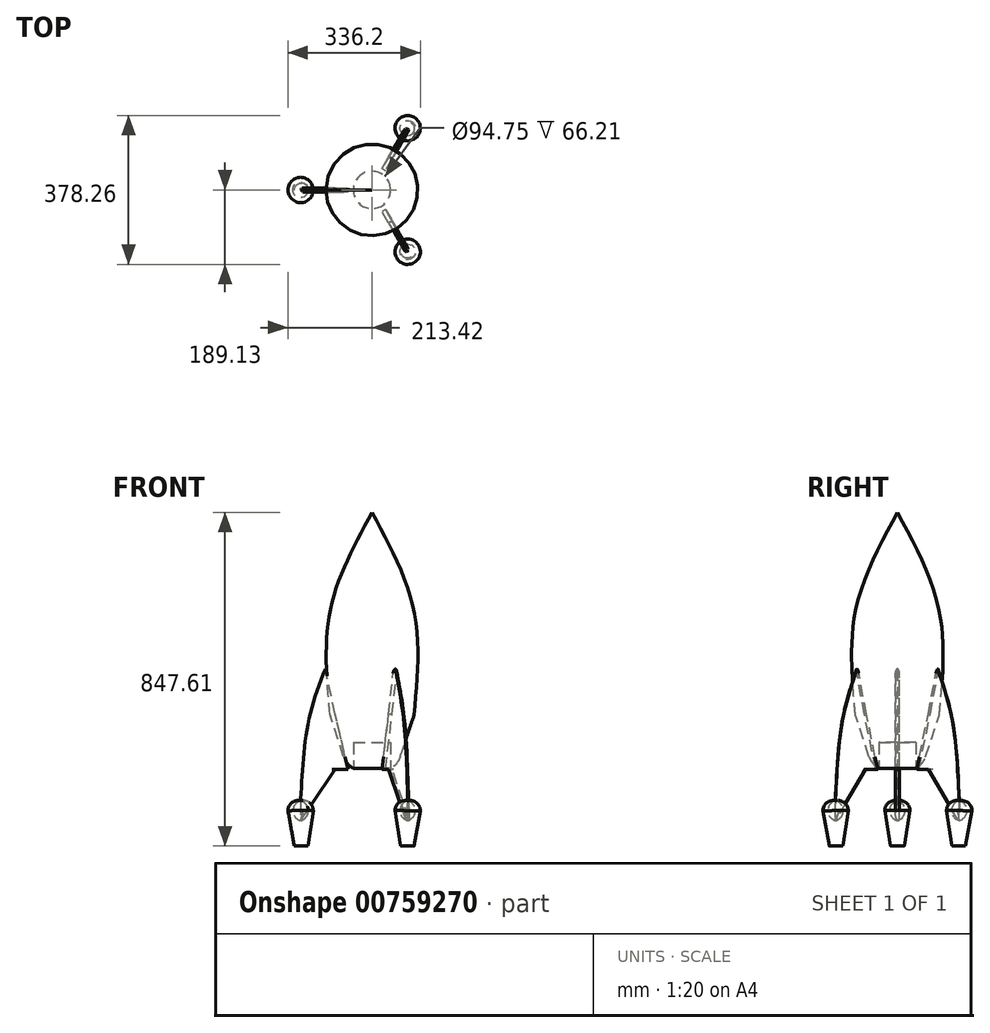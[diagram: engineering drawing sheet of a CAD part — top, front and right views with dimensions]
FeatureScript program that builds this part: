
annotation { "Feature Type Name" : "Feature", "Feature Type Description" : "" }
export const myFeature = defineFeature(function(context is Context, id is Id, definition is map)
    precondition{}
    {
        {
            var Q0;
            Q0=qCreatedBy(makeId("Front.planeOp"),FACE);
            var sketch = newSketch(context, id + "F0", { "sketchPlane" : qUnion([Q0])});
            skLineSegment(sketch, "E0", {"start": v(-61.86, -214.27) * mm, "end": v(-105.8, -81.4) * mm});
            skFitSpline(sketch, "E1", {"points": [v(-106.34, -79.78) * mm, v(-106.34, 186.1) * mm, v(0, 436.45) * mm], "startDerivative": vector(-52.57, 543.97) * mm, "endDerivative": vector(264.66, 488.59) * mm});
            skArc(sketch, "E2.filletArc", {"start": v(-106.5, -78.08) * mm, "mid": v(-106.25, -79.76) * mm, "end": v(-105.8, -81.4) * mm});
            skLineSegment(sketch, "E3", {"start": v(0, -148.06) * mm, "end": v(0, 436.45) * mm});
            skLineSegment(sketch, "E4", {"start": v(-61.86, -214.27) * mm, "end": v(-47.38, -214.27) * mm});
            skLineSegment(sketch, "E5", {"start": v(-47.38, -214.27) * mm, "end": v(-47.38, -148.06) * mm});
            skLineSegment(sketch, "E6", {"start": v(-47.38, -148.06) * mm, "end": v(0, -148.06) * mm});
            skPoint(sketch, "E7.orphan", {"position": v(0, -214.27) * mm});
            skSolve(sketch);
        }
        {
            var Q0;
            Q0 = qSketchRegion(id + "F0", true);
            var Q1;
            Q1=sQuery(id+"F0.wireOp",EDGE,"E3");
            revolve(context, id + "F1", {"surfaceOperationType" : NewSurfaceOperationType.NEW, "entities" : qUnion([Q0]), "axis" : qUnion([Q1]), "revolveType" : RevolveType.FULL});
        }
        {
            var Q0;
            Q0=qCreatedBy(makeId("Front.planeOp"),FACE);
            var sketch = newSketch(context, id + "F2", { "sketchPlane" : qUnion([Q0])});
            skFitSpline(sketch, "E8", {"points": [v(-118.68, 38.72) * mm, v(-161.16, -93.41) * mm, v(-181.6, -296.33) * mm], "startDerivative": vector(-106.76, -274.68) * mm, "endDerivative": vector(-21.8, -391.7) * mm});
            skArc(sketch, "E9", {"start": v(-181.6, -296.33) * mm, "mid": v(-206.93, -304.37) * mm, "end": v(-211.8, -330.49) * mm});
            skLineSegment(sketch, "E10", {"start": v(-213.42, -321.5) * mm, "end": v(-197.34, -411.16) * mm});
            skLineSegment(sketch, "E11", {"start": v(-197.34, -411.16) * mm, "end": v(-180.03, -411.16) * mm});
            skLineSegment(sketch, "E12", {"start": v(-180.03, -411.16) * mm, "end": v(-181.6, -296.33) * mm});
            skPoint(sketch, "E13.orphan", {"position": v(-181.6, -346.67) * mm});
            skLineSegment(sketch, "E14", {"start": v(-181.6, -346.67) * mm, "end": v(-93.52, -216.1) * mm});
            skLineSegment(sketch, "E15", {"start": v(-93.52, -216.1) * mm, "end": v(-60.48, -216.1) * mm});
            skLineSegment(sketch, "E16", {"start": v(-60.48, -216.1) * mm, "end": v(-93.52, -76.1) * mm});
            skLineSegment(sketch, "E17", {"start": v(-93.52, -76.1) * mm, "end": v(-118.68, 38.72) * mm});
            skSolve(sketch);
        }
        {
            var Q0;
            {var subQ4=sQuery(id+"F2.wireOp",EDGE,"E8");Q0=makeQuery(id+"F2.imprint","IMPRINT",FACE,{"disambiguationData":[TD([[makeQuery(id+"F2.imprint","IMPRINT",EDGE,{"derivedFrom":subQ4}),1.0]])]});}
            extrude(context, id + "F3", {"entities" : qUnion([Q0]), "endBound" : BoundingType.SYMMETRIC, "depth" : 10.16 * mm, "offsetDistance" : 25.4 * mm});
        }
        {
            var Q0;
            {var subQ0=sQuery(id+"F2.wireOp",EDGE,"E11");Q0=makeQuery(id+"F2.imprint","IMPRINT",FACE,{"disambiguationData":[TD([[makeQuery(id+"F2.imprint","IMPRINT",EDGE,{"derivedFrom":subQ0}),1.0]])]});}
            var Q1;
            Q1=sQuery(id+"F2.wireOp",EDGE,"E12");
            revolve(context, id + "F4", {"surfaceOperationType" : NewSurfaceOperationType.NEW, "entities" : qUnion([Q0]), "axis" : qUnion([Q1]), "revolveType" : RevolveType.FULL});
        }
        {
            var Q0;
            Q0=makeQuery(id+"F3.opExtrude","CAP_EDGE",EDGE,{"disambiguationData":[OSD([sQuery(id+"F2.wireOp",EDGE,"E8")])],"isStart":true});
            var Q1;
            Q1=makeQuery(id+"F3.opExtrude","CAP_EDGE",EDGE,{"disambiguationData":[OSD([sQuery(id+"F2.wireOp",EDGE,"E8")])],"isStart":false});
            var Q2;
            Q2=makeQuery(id+"F3.opExtrude","CAP_EDGE",EDGE,{"disambiguationData":[OSD([sQuery(id+"F2.wireOp",EDGE,"E14")])],"isStart":false});
            fillet(context, id + "F5", {"entities" : qUnion([Q0, Q1, Q2]), "radius" : 6.13 * mm, "tangentPropagation" : true, "allowEdgeOverflow" : false});
        }
        {
            var Q0;
            Q0=qCreatedBy(makeId("Top.planeOp"),FACE);
            var sketch = newSketch(context, id + "F6", { "sketchPlane" : qUnion([Q0])});
            skCircle(sketch, "E18", {"center": v(0, 0) * mm, "radius": 182.26 * mm});
            skSolve(sketch);
        }
        {
            var Q0;
            Q0=makeQuery(id+"F3.opExtrude","SWEPT_BODY",BODY,{"disambiguationData":[OSD([sQuery(id+"F2.wireOp",EDGE,"E8"),sQuery(id+"F2.wireOp",EDGE,"E12"),sQuery(id+"F2.wireOp",EDGE,"E14"),sQuery(id+"F2.wireOp",EDGE,"E15"),sQuery(id+"F2.wireOp",EDGE,"E16"),sQuery(id+"F2.wireOp",EDGE,"E17")])]});
            var Q1;
            Q1=makeQuery(id+"F4.opRevolve","SWEPT_BODY",BODY,{"disambiguationData":[OSD([sQuery(id+"F2.wireOp",EDGE,"E9"),sQuery(id+"F2.wireOp",EDGE,"E10"),sQuery(id+"F2.wireOp",EDGE,"E11"),sQuery(id+"F2.wireOp",EDGE,"E12")])]});
            var Q2;
            Q2=sQuery(id+"F6.wireOp",EDGE,"E18");
            circularPattern(context, id + "F7", {"entities" : qUnion([Q0, Q1]), "axis" : qUnion([Q2]), "angle" : 360 * degree, "instanceCount" : 3, "equalSpace" : true});
        }
        {
            var Q0;
            Q0=makeQuery(id+"F1.opRevolve","SWEPT_FACE",FACE,{"disambiguationData":[OSD([sQuery(id+"F0.wireOp",EDGE,"E0")])]});
            fillet(context, id + "F8", {"entities" : qUnion([Q0]), "radius" : 54.34 * mm, "tangentPropagation" : true, "allowEdgeOverflow" : false});
        }
    });
